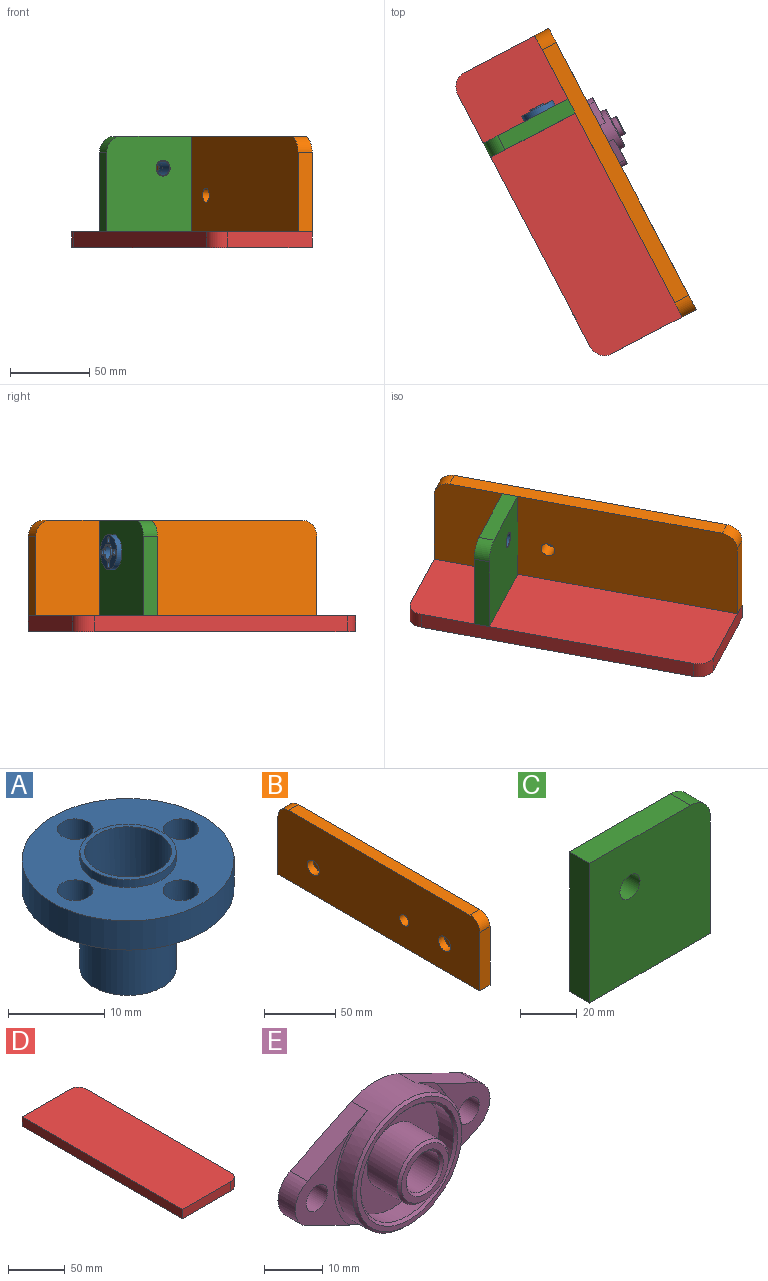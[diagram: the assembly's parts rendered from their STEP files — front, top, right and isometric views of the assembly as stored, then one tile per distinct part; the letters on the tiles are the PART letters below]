
ASSEMBLY  parts=5 mates=6
PART A: 12 faces, bbox 22x22x14.7 mm
  f0: cylinder r=11mm len=22mm, axis (0,0,-1), area 255.7mm2, adj f1,f2
  f1: plane 22x22mm, normal (0,0,1), area 258.6mm2, adj f0,f3,f8,f9,f10,f11
  f2: plane 22x22mm, normal (0,0,-1), area 258.6mm2, adj f0,f5,f8,f9,f10,f11
  f3: cylinder r=5mm len=10mm, axis (0,0,-1), area 31.4mm2, adj f1,f4
  f4: plane 10x10mm, normal (0,0,1), area 14.9mm2, adj f3,f7
  f5: cylinder r=5mm len=10mm, axis (0,0,1), area 314.2mm2, adj f2,f6
  f6: plane 10x10mm, normal (0,0,-1), area 14.9mm2, adj f5,f7
  f7: cylinder r=4.5mm len=14.7mm, axis (0,0,1), area 415.6mm2, adj f4,f6
  f8: cylinder r=1.85mm len=3.7mm, axis (0,0,1), area 43mm2, adj f1,f2
  f9: cylinder r=1.85mm len=3.7mm, axis (0,0,1), area 43mm2, adj f1,f2
  f10: cylinder r=1.85mm len=3.7mm, axis (0,0,1), area 43mm2, adj f1,f2
  f11: cylinder r=1.85mm len=3.7mm, axis (0,0,1), area 43mm2, adj f1,f2
PART B: 13 faces, bbox 10x200x60 mm
  f0: plane 180x10mm, normal (0,0,1), area 1800mm2, adj f1,f3,f6,f7
  f1: plane 200x60mm, normal (1,0,0), area 11893.5mm2, adj f0,f2,f4,f5,f6,f7,f8
  f2: plane 50x10mm, normal (0,1,0), area 500mm2, adj f1,f3,f5,f7
  f3: plane 200x60mm, normal (-1,0,0), area 11667.3mm2, adj f0,f2,f4,f5,f6,f7,f8,f9
  f4: plane 50x10mm, normal (0,-1,0), area 500mm2, adj f1,f3,f5,f6
  f5: plane 200x10mm, normal (0,0,-1), area 2000mm2, adj f1,f2,f3,f4
  f6: cylinder r=10mm len=10mm, axis (-1,0,0), area 157.1mm2, adj f0,f1,f3,f4
  f7: cylinder r=10mm len=10mm, axis (1,0,0), area 157.1mm2, adj f0,f1,f2,f3
  f8: cylinder r=4.5mm len=10mm, axis (-1,0,0), area 282.7mm2, adj f1,f3
  f9: cylinder r=6mm len=12mm, axis (-1,0,0), area 226.2mm2, adj f3,f10
  f10: plane 12x12mm, normal (-1,0,0), area 113.1mm2, adj f9
  f11: cylinder r=6mm len=12mm, axis (-1,0,0), area 226.2mm2, adj f3,f12
  f12: plane 12x12mm, normal (-1,0,0), area 113.1mm2, adj f11
PART C: 8 faces, bbox 60x10x60 mm
  f0: plane 50x10mm, normal (0,0,1), area 500mm2, adj f1,f4,f5,f6
  f1: plane 60x60mm, normal (0,-1,0), area 3500mm2, adj f0,f2,f3,f4,f6,f7
  f2: plane 60x10mm, normal (0,0,-1), area 600mm2, adj f1,f3,f4,f5
  f3: plane 50x10mm, normal (1,0,0), area 500mm2, adj f1,f2,f5,f6
  f4: plane 60x10mm, normal (-1,0,0), area 600mm2, adj f0,f1,f2,f5
  f5: plane 60x60mm, normal (0,1,0), area 3500mm2, adj f0,f2,f3,f4,f6,f7
  f6: cylinder r=10mm len=10mm, axis (0,-1,0), area 157.1mm2, adj f0,f1,f3,f5
  f7: cylinder r=5mm len=10mm, axis (0,-1,0), area 314.2mm2, adj f1,f5
PART D: 8 faces, bbox 70x200x10 mm
  f0: plane 60x10mm, normal (0,1,0), area 600mm2, adj f3,f4,f5,f6
  f1: plane 180x10mm, normal (1,0,0), area 1800mm2, adj f4,f5,f6,f7
  f2: plane 60x10mm, normal (0,-1,0), area 600mm2, adj f3,f4,f5,f7
  f3: plane 200x10mm, normal (-1,0,0), area 2000mm2, adj f0,f2,f4,f5
  f4: plane 200x70mm, normal (0,0,1), area 13957.1mm2, adj f0,f1,f2,f3,f6,f7
  f5: plane 200x70mm, normal (0,0,-1), area 13957.1mm2, adj f0,f1,f2,f3,f6,f7
  f6: cylinder r=10mm len=10mm, axis (0,0,-1), area 157.1mm2, adj f0,f1,f4,f5
  f7: cylinder r=10mm len=10mm, axis (0,0,1), area 157.1mm2, adj f1,f2,f4,f5
PART E: 26 faces, bbox 47.2x12x26.5 mm
  f0: plane 22.5x22.5mm, normal (0,-1,0), area 276.8mm2, adj f18,f20
  f1: plane 19.24x13.09mm, normal (0,-1,0), area 94.3mm2, adj f2,f7,f9,f10,f15
  f2: plane 14.88x7.24mm, normal (-0.44,0,-0.9), area 67.9mm2, adj f1,f3,f9,f13,f14,f15
  f3: cylinder r=13.25mm len=26.5mm, axis (0,1,0), area 410mm2, adj f2,f4,f6,f7,f13,f14,f16,f22
  f4: plane 14.88x7.24mm, normal (0.44,0,-0.9), area 67.9mm2, adj f3,f5,f12,f13,f16,f17
  f5: cylinder r=5.2mm len=9.35mm, axis (0,1,0), area 48.8mm2, adj f4,f6,f12,f13
  f6: plane 14.88x7.24mm, normal (0.44,0,0.9), area 67.9mm2, adj f3,f5,f12,f13,f16,f17
  f7: plane 14.88x7.24mm, normal (-0.44,0,0.9), area 67.9mm2, adj f1,f3,f9,f13,f14,f15
  f8: cylinder r=4mm len=11.5mm, axis (0,1,0), area 289mm2, adj f13,f25
  f9: cylinder r=5.2mm len=9.35mm, axis (0,1,0), area 48.8mm2, adj f1,f2,f7,f13
  f10: cylinder r=2.6mm len=5.2mm, axis (0,1,0), area 68.6mm2, adj f1,f13
  f11: cylinder r=2.6mm len=5.2mm, axis (0,1,0), area 68.6mm2, adj f12,f13
  f12: plane 19.24x13.09mm, normal (0,-1,0), area 94.3mm2, adj f4,f5,f6,f11,f17
  f13: plane 47.2x26.5mm, normal (0,1,0), area 737.2mm2, adj f2,f3,f4,f5,f6,f7,f8,f9
  f14: plane 23.83x8.45mm, normal (0,-1,0), area 23.7mm2, adj f2,f3,f7,f15
  f15: cylinder r=14.25mm len=19.24mm, axis (0,-1,0), area 6.3mm2, adj f1,f2,f7,f14
  f16: plane 23.83x8.45mm, normal (0,-1,0), area 23.7mm2, adj f3,f4,f6,f17
  f17: cylinder r=14.25mm len=19.24mm, axis (0,-1,0), area 6.3mm2, adj f4,f6,f12,f16
  f18: cylinder r=6.2mm len=12.4mm, axis (0,1,0), area 284.4mm2, adj f0,f24
  f19: plane 11.4x11.4mm, normal (0,-1,0), area 38.5mm2, adj f24,f25
  f20: cylinder r=11.25mm len=22.5mm, axis (0,1,0), area 247.4mm2, adj f0,f23
  f21: plane 25.5x25.5mm, normal (0,-1,0), area 77mm2, adj f22,f23
  f22: cone r=12.75mm half-angle=45deg, axis (0,1,0), area 57.8mm2, adj f3,f21
  f23: cone r=11.25mm half-angle=45deg, axis (0,-1,0), area 51.1mm2, adj f20,f21
  f24: cone r=5.7mm half-angle=45deg, axis (0,1,0), area 26.4mm2, adj f18,f19
  f25: cone r=4mm half-angle=45deg, axis (0,-1,0), area 18.9mm2, adj f8,f19
PLACE A rot(axis=(-0.94,-0.23,0.23),93.3deg) t=(100.31,79.83,67.15)mm
PLACE B rot(axis=(0,0,-1),152.3deg) t=(152.41,45.05,27.15)mm
PLACE C rot(axis=(0,0,-1),152.3deg) t=(152.41,45.05,27.15)mm
PLACE D rot(axis=(0,0,-1),152.3deg) t=(152.41,45.05,27.15)mm
PLACE E rot(axis=(0,0,1),117.7deg) t=(140.81,67.19,50.15)mm
MATE fastened C.f7 <-> A.f0  axis (-0.46,0.89,0) through (100.31,79.83,67.15)mm
MATE planar C.f2 <-> D.f4  axis (0,0,-1) through (93.77,70.76,27.15)mm
MATE fastened B.f4 <-> D.f2  axis (-0.46,0.89,0) through (105.98,133.62,27.15)mm
MATE parallel D.f2 <-> C.f1  axis (-0.46,0.89,0) through (79.41,119.69,22.15)mm
MATE planar B.f1 <-> C.f4  axis (-0.89,-0.46,0) through (143.62,40.29,57.09)mm
MATE fastened B.f8 <-> E.f3  axis (0.89,0.46,0) through (140.81,67.19,50.15)mm
